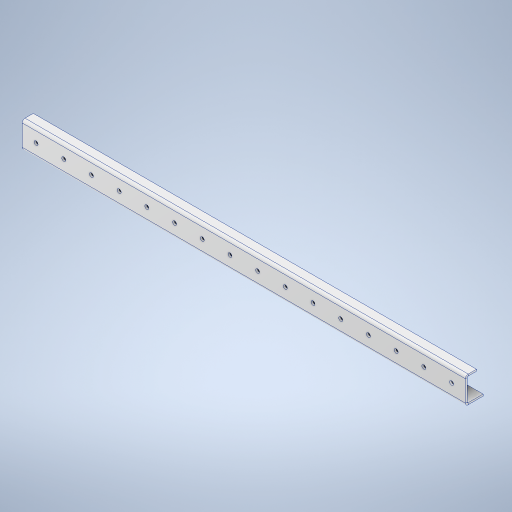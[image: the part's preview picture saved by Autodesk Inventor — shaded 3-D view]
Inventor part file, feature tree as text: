
AUTODESK INVENTOR PART (.ipt)
format: ipt  version: 2024 (Build 280153000, 153)  size: 417,280 bytes
history: native  units: mm
features: sheet_metal_op x7, sketch x4, fillet x3, other x3, extrude x2, hole x1
ambient origin geometry x8: Origin, YZ Plane, XZ Plane, XY Plane, X Axis, Y Axis, Z Axis, Center Point
bodies: Body1 (feature_tree)
feature tree (20):
  sheet_metal_op  "Face2"
  sheet_metal_op  "Flange3"
  sheet_metal_op  "Flange4"
  hole  "Hole3"  [1 undecoded]
  sketch  "Sketch9"  dims[d76=10.0mm d77=90.0deg d78=0.889mm d79=6.4008mm d80=1.6002mm d81=0.889mm d82=1.6002mm d83=0.8001mm d84=3.2004mm d85=0.889mm d86=16.0mm d87=90.0deg d88=0.889mm d89=6.4008mm d90=1.6002mm d91=0.889mm d92=160.0mm d94=25.0mm d95=10.0mm d97=10.0mm d99=3.5mm d100=6.0mm d101=3.023mm d102=2.0mm d103=14.3117mm d104=1.6002mm d105=20.594885mm d106=20.0mm d107=19.5mm d110=2.333333mm d111=2.333333mm d112=1.166667mm d113=1.166667mm d114=14.0mm d115=22.0mm d116=100.0mm d117=120.0deg d118=120.0deg d119=10.0mm d120=0.0mm d121=10.0mm d122=0.0mm d123=2.0mm d124=0.3mm d125=0.6mm d126=0.872665mm]
  extrude  "Extrusion5"  Depth=1.6002mm
  extrude  "Extrusion6"  Depth=0.889mm
  fillet  "Fillet4"  Radius=3.2004mm
  fillet  "Fillet6"  Radius=0.889mm
  fillet  "Fillet5"  Radius=6.4008mm
  other  "Plate4"
  sketch  "Sketch6"  dims[d10=36.0mm d14=15.0mm d69=400.0mm]
  other  "Plate5"
  sheet_metal_op  "Bend3"
  sheet_metal_op  "Corner3"
  sketch  "Sketch7"  dims[d70=24.0mm d71=1.6002mm]
  other  "Plate6"
  sheet_metal_op  "Bend4"
  sheet_metal_op  "Corner4"
  sketch  "Sketch8"  dims[d72=1.6002mm d73=0.8001mm d74=3.2004mm d75=0.889mm]
note: 1 required parameter value undecoded (feature->parameter linkage not recoverable at this tier; creation-order binding heuristic only, values carry confidence <= 0.55)
